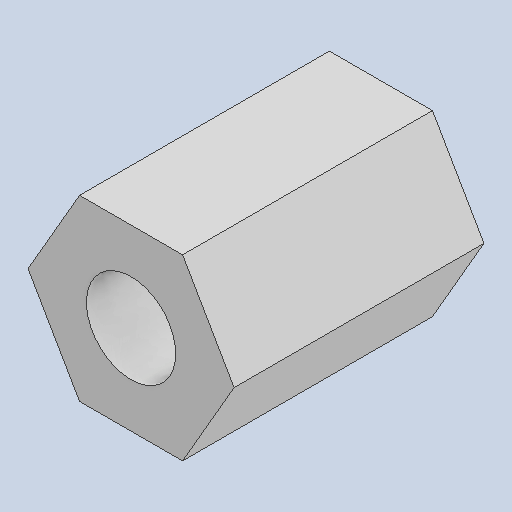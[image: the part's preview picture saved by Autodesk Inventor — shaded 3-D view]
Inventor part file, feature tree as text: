
AUTODESK INVENTOR PART (.ipt)
format: ipt  version: 2024.2 (Build 282272000, 272)  size: 101,376 bytes
history: native  units: mm
features: extrude x2, sketch x1
ambient origin geometry x8: Origin, YZ Plane, XZ Plane, XY Plane, X Axis, Y Axis, Z Axis, Center Point
bodies: Solid1 (feature_tree)
feature tree (3):
  extrude  "Extrusion1"  Depth=7.0mm TaperAngle=0.0deg
  extrude  "Extrusion3"  Depth=7.0mm
  sketch  "Sketch1"  dims[d0=5.0mm d1=7.0mm d2=0.0mm d6=2.5mm d7=7.0mm d8=0.0mm]
